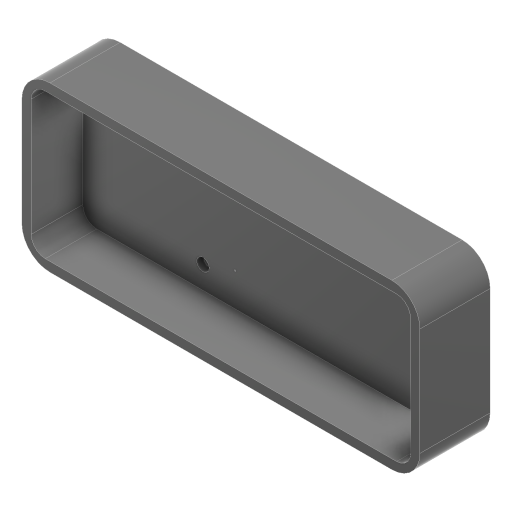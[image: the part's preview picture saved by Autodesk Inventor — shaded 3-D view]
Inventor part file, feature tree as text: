
AUTODESK INVENTOR PART (.ipt)
format: ipt  version: 2023.2 (Build 272271000, 271)  size: 266,752 bytes
history: native  units: mm
features: extrude x3, sketch x2, projected_geometry x1
ambient origin geometry x8: Origin, YZ Plane, XZ Plane, XY Plane, X Axis, Y Axis, Z Axis, Center Point
bodies: Solid1 (feature_tree)
feature tree (6):
  sketch  "Sketch1"  dims[d0=2.5mm d1=0.0mm d2=85.0mm]
  extrude  "Extrusion1"  Depth=85.0mm
  extrude  "Extrusion2"  Depth=6.0mm
  extrude  "Extrusion3"  Depth=81.0mm
  sketch  "Sketch3"  dims[d3=35.0mm d4=6.0mm d5=81.0mm d6=31.0mm d7=3.0mm d8=3.0mm d9=15.0mm d10=0.0mm d11=4.0mm d12=0.0mm]
  projected_geometry  "Projected Loop2"
